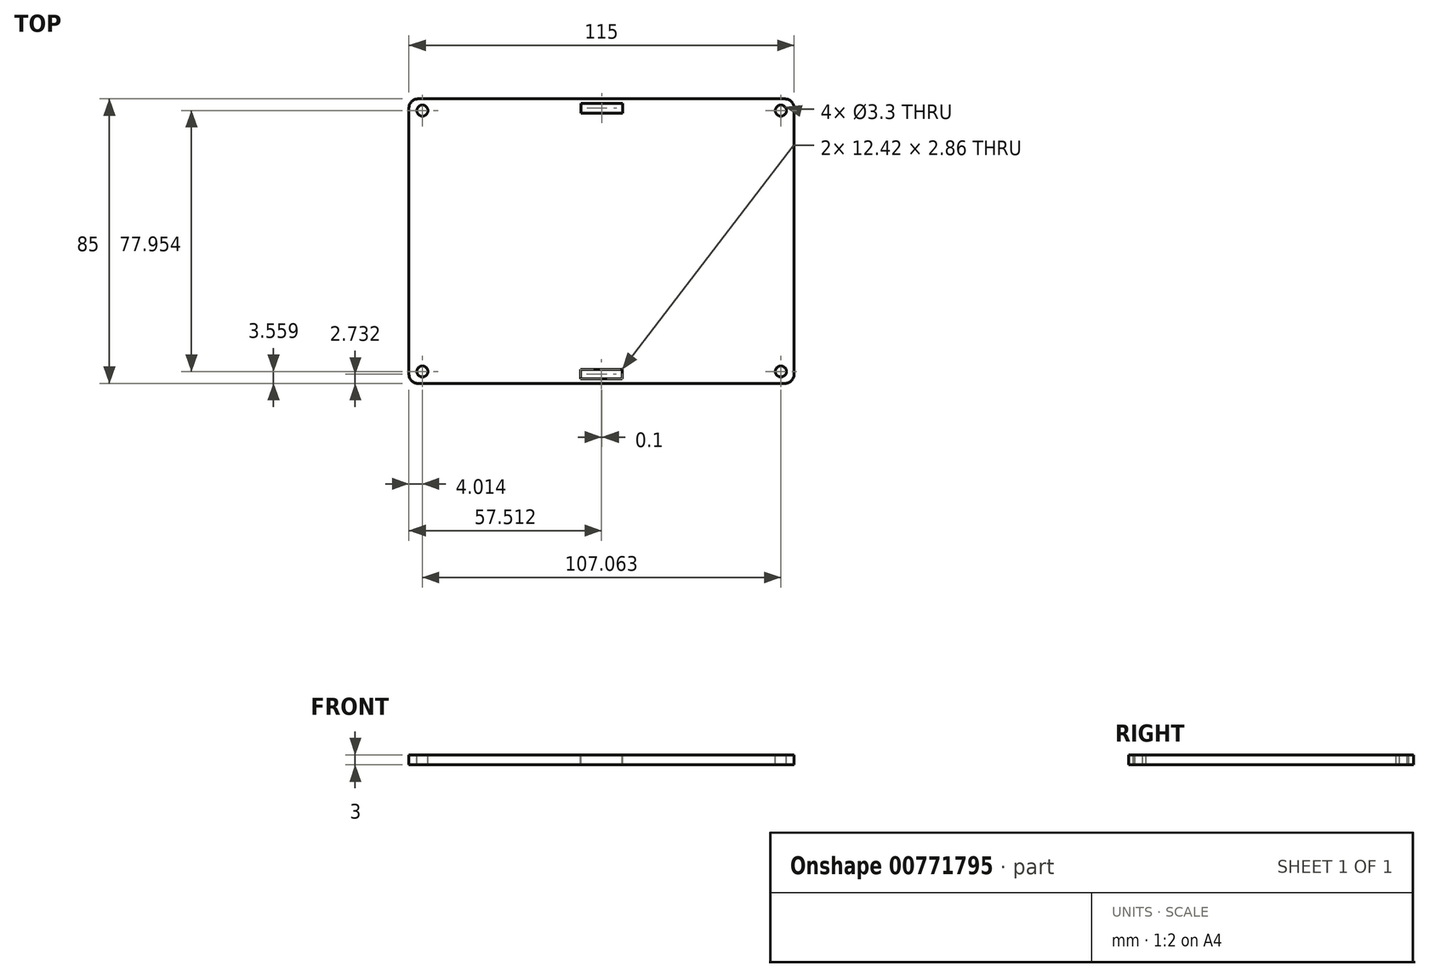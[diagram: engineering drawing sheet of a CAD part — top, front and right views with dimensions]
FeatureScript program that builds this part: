
annotation { "Feature Type Name" : "Feature", "Feature Type Description" : "" }
export const myFeature = defineFeature(function(context is Context, id is Id, definition is map)
    precondition{}
    {
        {
            var Q0;
            Q0=qCreatedBy(makeId("Top.planeOp"),FACE);
            var sketch = newSketch(context, id + "F0", { "sketchPlane" : qUnion([Q0])});
            skLineSegment(sketch, "E0.bottom", {"start": v(57.5, -42.5) * mm, "end": v(-57.5, -42.5) * mm});
            skLineSegment(sketch, "E0.top", {"start": v(57.5, 42.5) * mm, "end": v(-57.5, 42.5) * mm});
            skLineSegment(sketch, "E0.left", {"start": v(57.5, -42.5) * mm, "end": v(57.5, 42.5) * mm});
            skLineSegment(sketch, "E0.right", {"start": v(-57.5, -42.5) * mm, "end": v(-57.5, 42.5) * mm});
            skPoint(sketch, "E0.middle", {"position": v(0, 0) * mm});
            skPoint(sketch, "E1", {"position": v(-53.49, 39.01) * mm});
            skPoint(sketch, "E2", {"position": v(-53.49, -38.94) * mm});
            skPoint(sketch, "E3", {"position": v(53.58, -38.94) * mm});
            skPoint(sketch, "E4", {"position": v(53.58, 39.01) * mm});
            skPoint(sketch, "E5.MirrorP", {"position": v(-54.64, 0) * mm});
            skPoint(sketch, "E6.MirrorP", {"position": v(54.61, -0.05) * mm});
            skLineSegment(sketch, "E7.bottom", {"start": v(-6.2, -41.2) * mm, "end": v(-6.2, -38.34) * mm});
            skLineSegment(sketch, "E7.top", {"start": v(6.22, -41.2) * mm, "end": v(6.22, -38.34) * mm});
            skLineSegment(sketch, "E7.left", {"start": v(-6.2, -41.2) * mm, "end": v(6.22, -41.2) * mm});
            skLineSegment(sketch, "E7.right", {"start": v(-6.2, -38.34) * mm, "end": v(6.22, -38.34) * mm});
            skPoint(sketch, "E7.middle", {"position": v(0.01, -39.77) * mm});
            skLineSegment(sketch, "E8.MirrorCS", {"start": v(6.22, -41.2) * mm, "end": v(-6.2, -41.2) * mm});
            skLineSegment(sketch, "E9.MirrorCS", {"start": v(6.22, -38.34) * mm, "end": v(-6.2, -38.34) * mm});
            skLineSegment(sketch, "E10.bottom", {"start": v(-6.1, 38.3) * mm, "end": v(-6.1, 41.16) * mm});
            skLineSegment(sketch, "E10.top", {"start": v(6.32, 38.3) * mm, "end": v(6.32, 41.16) * mm});
            skLineSegment(sketch, "E10.left", {"start": v(-6.1, 38.3) * mm, "end": v(6.32, 38.3) * mm});
            skLineSegment(sketch, "E10.right", {"start": v(-6.1, 41.16) * mm, "end": v(6.32, 41.16) * mm});
            skPoint(sketch, "E10.middle", {"position": v(0.11, 39.73) * mm});
            skLineSegment(sketch, "E11.MirrorCS", {"start": v(6.32, 38.3) * mm, "end": v(-6.1, 38.3) * mm});
            skLineSegment(sketch, "E12.MirrorCS", {"start": v(6.32, 41.16) * mm, "end": v(-6.1, 41.16) * mm});
            skSolve(sketch);
        }
        {
            var Q0;
            Q0=makeQuery(id+"F0.imprint","IMPRINT",FACE,{"disambiguationData":[TD([[makeQuery(id+"F0.imprint","IMPRINT",EDGE,{"derivedFrom":sQuery(id+"F0.wireOp",EDGE,"E0.bottom")}),-1.0]])]});
            extrude(context, id + "F1", {"entities" : qUnion([Q0]), "oppositeDirection" : true, "depth" : 3 * mm, "offsetDistance" : 25 * mm});
        }
        {
            var Q0;
            Q0=makeQuery(id+"F1.opExtrude","SWEPT_EDGE",EDGE,{"disambiguationData":[OSD([sQuery(id+"F0.wireOp",EDGE,"E0.bottom"),sQuery(id+"F0.wireOp",EDGE,"E0.left")])]});
            var Q1;
            Q1=makeQuery(id+"F1.opExtrude","SWEPT_EDGE",EDGE,{"disambiguationData":[OSD([sQuery(id+"F0.wireOp",EDGE,"E0.top"),sQuery(id+"F0.wireOp",EDGE,"E0.left")])]});
            var Q2;
            Q2=makeQuery(id+"F1.opExtrude","SWEPT_EDGE",EDGE,{"disambiguationData":[OSD([sQuery(id+"F0.wireOp",EDGE,"E0.bottom"),sQuery(id+"F0.wireOp",EDGE,"E0.right")])]});
            var Q3;
            Q3=makeQuery(id+"F1.opExtrude","SWEPT_EDGE",EDGE,{"disambiguationData":[OSD([sQuery(id+"F0.wireOp",EDGE,"E0.top"),sQuery(id+"F0.wireOp",EDGE,"E0.right")])]});
            fillet(context, id + "F2", {"entities" : qUnion([Q0, Q1, Q2, Q3]), "radius" : 2.66 * mm, "tangentPropagation" : true, "allowEdgeOverflow" : false});
        }
        {
            var Q0;
            Q0=sQuery(id+"F0.wireOp",VERTEX,"E2");
            var Q1;
            Q1=sQuery(id+"F0.wireOp",VERTEX,"E1");
            var Q2;
            Q2=sQuery(id+"F0.wireOp",VERTEX,"E3");
            var Q3;
            Q3=sQuery(id+"F0.wireOp",VERTEX,"E4");
            var Q4;
            Q4=makeQuery(id+"F1.opExtrude","SWEPT_BODY",BODY,{"disambiguationData":[OSD([sQuery(id+"F0.wireOp",EDGE,"E0.bottom"),sQuery(id+"F0.wireOp",EDGE,"E0.top"),sQuery(id+"F0.wireOp",EDGE,"E0.left"),sQuery(id+"F0.wireOp",EDGE,"E0.right")])]});
            hole(context, id + "F3", {"style" : HoleStyle.SIMPLE, "endStyle" : HoleEndStyle.BLIND, "standardTappedOrClearance" : lookupTablePath({ "standard" : "ISO", "fit" : "Normal", "size" : "M3", "type" : "Clearance" }), "standardBlindInLast" : lookupTablePath({ "fit" : "Standard", "standard" : "ISO", "size" : "M3", "type" : "Clearance" }), "holeDiameter" : 3.3 * mm, "majorDiameter" : 3 * mm, "holeDepth" : 13.5 * mm, "isTappedThrough" : true, "tappedDepth" : 12 * mm, "tapClearance" : 3, "locations" : qUnion([Q0, Q1, Q2, Q3]), "scope" : qUnion([Q4])});
        }
    });
